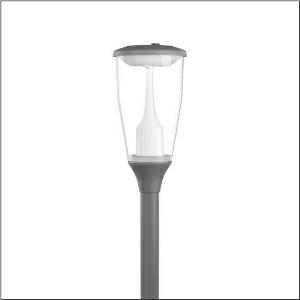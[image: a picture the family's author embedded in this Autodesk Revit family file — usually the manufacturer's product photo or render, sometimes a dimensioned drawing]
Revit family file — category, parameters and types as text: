
# Revit family: dl_11_iq___st1_2a_5xa5565ev14hp00022_f5ed
name_source: partatom
category: Lighting Fixtures
units: mm (PartAtom-declared; Revit-internal decimal feet)

## family parameters
Cut with Voids When Loaded = No
Host = Face
Light Source = No
Part Type = Normal
Room Calculation Point = No
Round Connector Dimension = Use Diameter
Shared = No

## types (1)
- --- (1 x LED, 4790 lm, 33.5 W, 3000K)
    Apparent Load = 34 VA
    CIE Flux Codes = 23 60 93 95 100
    Color Rendering = 70
    Color Temperature = 3000K
    Default Elevation = 1800 mm
    Description = DL 11 iQ, mast luminaire, Module 540 iQ-SR, primary light control with 3 zone facetted reflector, of plastic, silver coated, highly specular, structured, primary optical cover: cover, of PMMA, transparent, light distribution: ST1.2a, light emission: direct distribution, primary light characteristic: asymmetric, installation type: post-top, LED, High Power LED, rated luminous flux: 4.790lm, luminous efficacy: 143lm/W, light colour: 730, colour temperature: 3000K, control gear: iQ-Street Remote, D4i with power reduction, control: pre-setting: logarithmic dimming characteristic, Street-Remote, Auto-Match, Temp-Guard, Lumen-Switch, Night-Set, Smart-Wire, Light-Fading, Desk-Remote (wireless, voltage-free reading and setting of iQ features in the workshop via application-optimized NFC function/RFID function), optimised constant luminous flux control (CLO 2.0), mains connection: 220..240V, AC, 50/60Hz, connection cable pre-assembled, cable length: 5,5m, start of lifetime: 34W, end of service life: 36W, reduction: 15W, luminaire housing, upper part, of diecast aluminium, coated, SITECO metallic grey (DB 702S), spigot size: 60mm (post-top), mounting height: 3..5m, post-top mast mounting element, of diecast aluminium, coated, SITECO metallic grey (DB 702S), Module 540 iQ-SR, traffic white (RAL 9016), equipment: Power, Smart Interface above, protection rating (complete): IP66, insulation class (complete): insulation class II (safety insulation), certification: CE, ENEC, ENEC+, VDE, impact resistance: IK07, packaging unit: 1 piece

Light Distribution: ST1.2a
    Height = 665 mm
    Lamp = 1 x LED
    Lamp Light Flux = 4790 lm
    Lamp Power = 33.5 W
    Lamp count = 1
    Length = 334 mm
    Luminous efficacy = 143 lm/W
    Manufacturer = Siteco
    ModVariant = No
    Model = 5XA5565EV14HP00022
    Number of Poles = 1
    OnlyDefault = Yes
    Power Factor = 1
    Product Name = DL 11 iQ | ST1.2a
    Product group = mast luminaire | pylon top
    ProductGroupID = 6100
    Protection Class = Protection class II
    Protection Degree = IP 66
    RLX_Detail_Level = 1
    RLX_Emergency_Light_Flux = 0 lm
    RLX_Emergency_Type = 0
    RLX_Emergency_Type_DB = No
    RlxData = <blob elided: 160045 chars, md5=9eae6fbc>
    Socket = socket
    Standby Power = 0 W
    System Light Flux = 4790 lm
    System Power = 34 W
    Type Comments = factory setting: luminous flux: 100 % | dim-lin: 254 | 695 mA
    Type Image = l_1337541.jpg
    URL = http://relux.com
    VarID = @adj_040615
    Voltage = 0 V
    Weight = 0.00 kg
    Width = 0 mm  [stored 0 ft]

note: [stored X ft] marks values corroborated as IEEE doubles in the binary element streams (Revit-internal decimal feet)

## geometry (parser evidence)
native form markers: Blend x4, Sweep x12
no freeform markers — native parametric forms only
